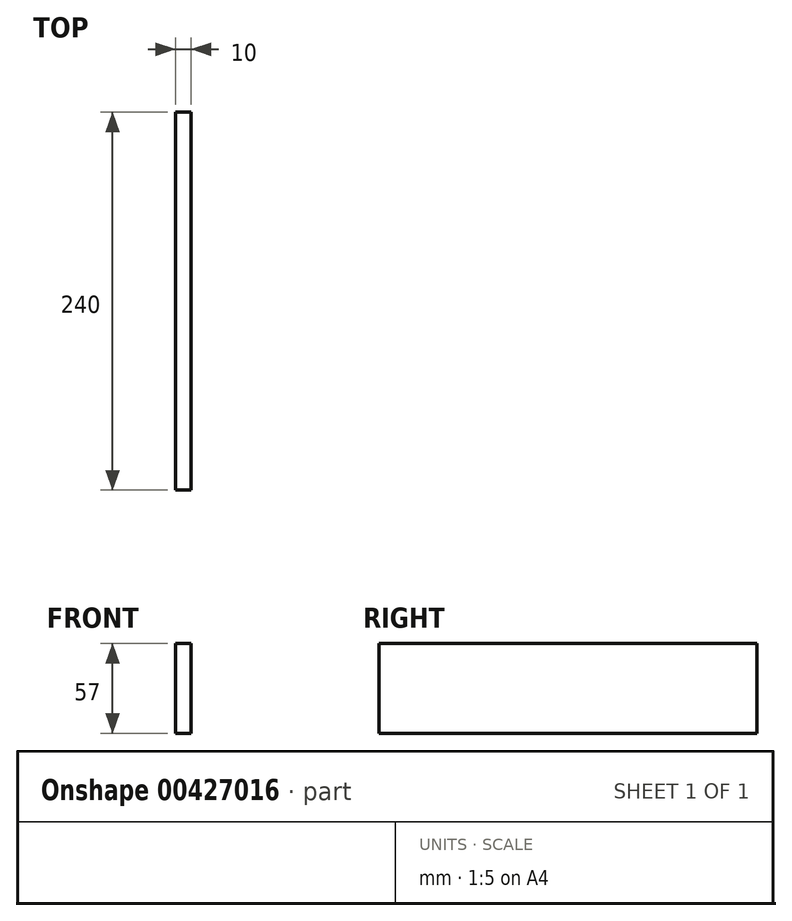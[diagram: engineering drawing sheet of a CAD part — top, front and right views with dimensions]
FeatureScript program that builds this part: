
annotation { "Feature Type Name" : "Feature", "Feature Type Description" : "" }
export const myFeature = defineFeature(function(context is Context, id is Id, definition is map)
    precondition{}
    {
        {
            var Q0;
            Q0=qCreatedBy(makeId("Front.planeOp"),FACE);
            var sketch = newSketch(context, id + "F0", { "sketchPlane" : qUnion([Q0])});
            skLineSegment(sketch, "E0.bottom", {"start": v(0, 0) * mm, "end": v(10, 0) * mm});
            skLineSegment(sketch, "E0.top", {"start": v(0, 57) * mm, "end": v(10, 57) * mm});
            skLineSegment(sketch, "E0.left", {"start": v(0, 0) * mm, "end": v(0, 57) * mm});
            skLineSegment(sketch, "E0.right", {"start": v(10, 0) * mm, "end": v(10, 57) * mm});
            skSolve(sketch);
        }
        {
            var Q0;
            Q0=makeQuery(id+"F0.imprint","IMPRINT",FACE,{"disambiguationData":[TD([[makeQuery(id+"F0.imprint","IMPRINT",EDGE,{"derivedFrom":sQuery(id+"F0.wireOp",EDGE,"E0.bottom")}),1.0]])]});
            extrude(context, id + "F1", {"entities" : qUnion([Q0]), "endBound" : BoundingType.SYMMETRIC, "offsetDistance" : 25 * mm, "depth" : 240 * mm});
        }
    });
